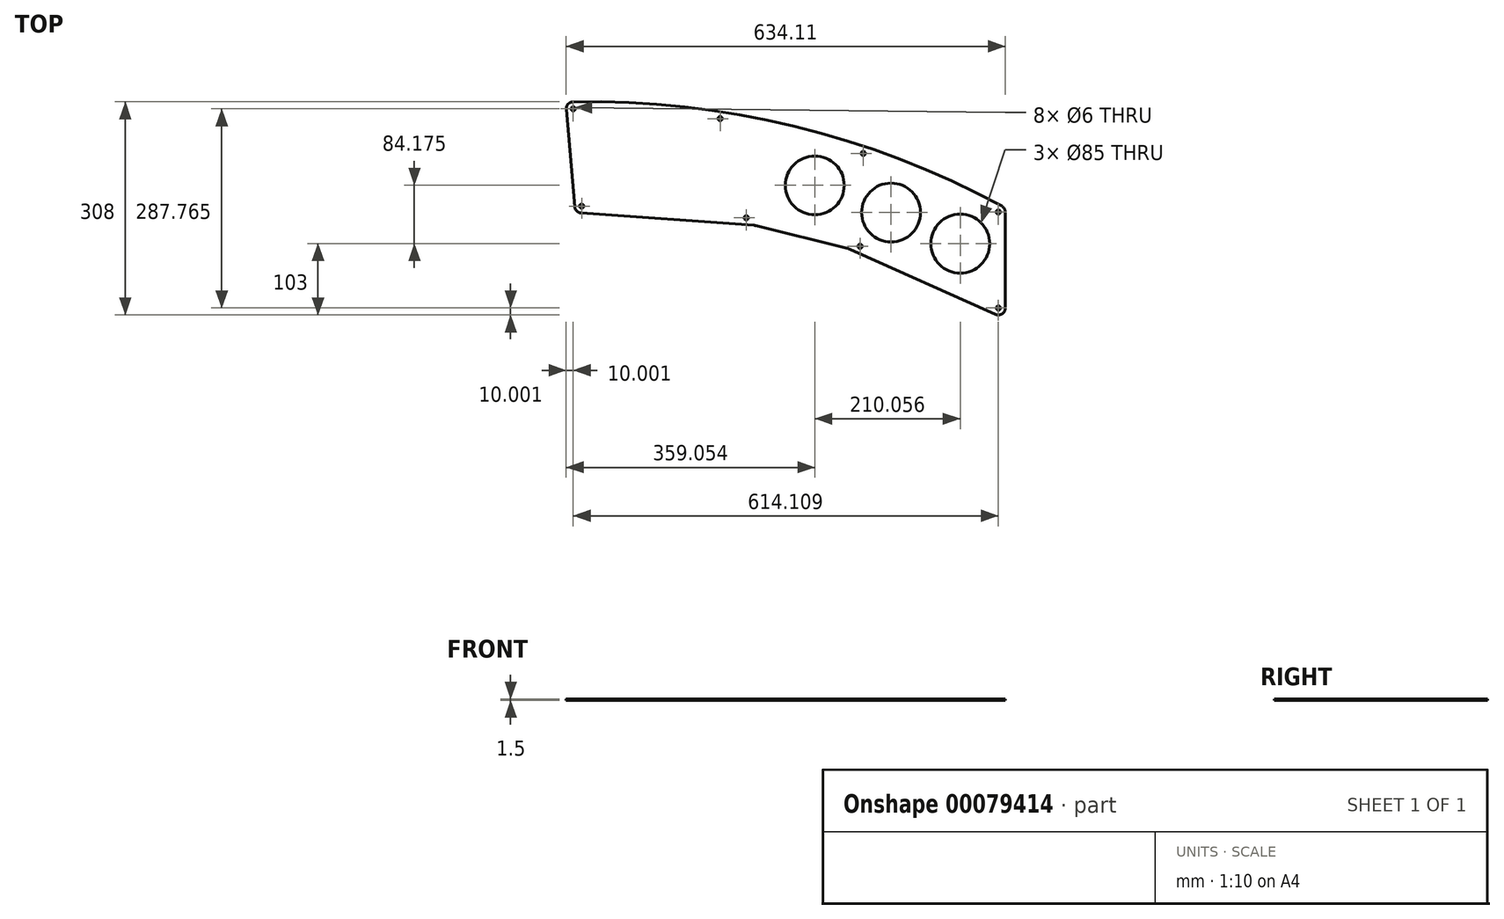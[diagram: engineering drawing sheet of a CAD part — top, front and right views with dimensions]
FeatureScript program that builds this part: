
annotation { "Feature Type Name" : "Feature", "Feature Type Description" : "" }
export const myFeature = defineFeature(function(context is Context, id is Id, definition is map)
    precondition{}
    {
        {
            var Q0;
            Q0=qCreatedBy(makeId("Top.planeOp"),FACE);
            var sketch = newSketch(context, id + "F0", { "sketchPlane" : qUnion([Q0])});
            skLineSegment(sketch, "E0", {"start": v(0, 450) * mm, "end": v(-635, 450) * mm});
            skLineSegment(sketch, "E1", {"start": v(-635, 450) * mm, "end": v(-635, 0) * mm});
            skLineSegment(sketch, "E2", {"start": v(-635, 0) * mm, "end": v(0, 0) * mm});
            skLineSegment(sketch, "E3", {"start": v(0, 0) * mm, "end": v(0, 450) * mm});
            skCircle(sketch, "E4", {"center": v(-600, -900) * mm, "radius": 1070 * mm});
            skCircle(sketch, "E5", {"center": v(-600, -900) * mm, "radius": 1250 * mm});
            skLineSegment(sketch, "E6", {"start": v(-621.03, 189.8) * mm, "end": v(-361.68, 171.41) * mm});
            skLineSegment(sketch, "E7", {"start": v(-361.68, 171.41) * mm, "end": v(-225.87, 137.41) * mm});
            skLineSegment(sketch, "E8", {"start": v(-225.87, 137.41) * mm, "end": v(0, 36.59) * mm});
            skPoint(sketch, "E9", {"position": v(0, 196.59) * mm});
            skLineSegment(sketch, "E10", {"start": v(-621.03, 189.8) * mm, "end": v(-635, 349.5) * mm});
            skSolve(sketch);
        }
        {
            var Q0;
            {var subQ8=sQuery(id+"F0.wireOp",EDGE,"E6");Q0=makeQuery(id+"F0.imprint","IMPRINT",FACE,{"disambiguationData":[TD([[makeQuery(id+"F0.imprint","IMPRINT",EDGE,{"derivedFrom":subQ8}),1.0]])]});}
            extrude(context, id + "F1", {"entities" : qUnion([Q0]), "depth" : 1.5 * mm});
        }
        {
            var Q0;
            Q0=makeQuery(id+"F1.opExtrude","CAP_FACE",FACE,{"disambiguationData":[OSD([sQuery(id+"F0.wireOp",EDGE,"E0"),sQuery(id+"F0.wireOp",EDGE,"E1"),sQuery(id+"F0.wireOp",EDGE,"E2"),sQuery(id+"F0.wireOp",EDGE,"NxOAb0fC-KCtt-g6Ye-Zb5N-PQVgE4h8CR18"),sQuery(id+"F0.wireOp",EDGE,"E3"),sQuery(id+"F0.wireOp",EDGE,"E4")])],"isStart":false});
            var sketch = newSketch(context, id + "F2", { "sketchPlane" : qUnion([Q0])});
            skCircle(sketch, "E11", {"center": v(-65, 145) * mm, "radius": 42.5 * mm});
            skCircle(sketch, "E12", {"center": v(-165, 190) * mm, "radius": 42.5 * mm});
            skCircle(sketch, "E13", {"center": v(-275.06, 229.18) * mm, "radius": 42.5 * mm});
            skLineSegment(sketch, "E14", {"start": v(-293.77, 154.41) * mm, "end": v(-256.83, 301.97) * mm, "construction": true});
            skCircle(sketch, "E15", {"center": v(-600, -900) * mm, "radius": 1175 * mm, "construction": true});
            skSolve(sketch);
        }
        {
            var Q0;
            Q0=makeQuery(id+"F2.imprint","IMPRINT",FACE,{"disambiguationData":[TD([[makeQuery(id+"F2.imprint","IMPRINT",EDGE,{"derivedFrom":sQuery(id+"F2.wireOp",EDGE,"E13")}),1.0]])]});
            var Q1;
            Q1=makeQuery(id+"F2.imprint","IMPRINT",FACE,{"disambiguationData":[TD([[makeQuery(id+"F2.imprint","IMPRINT",EDGE,{"derivedFrom":sQuery(id+"F2.wireOp",EDGE,"E12")}),1.0]])]});
            var Q2;
            Q2=makeQuery(id+"F2.imprint","IMPRINT",FACE,{"disambiguationData":[TD([[makeQuery(id+"F2.imprint","IMPRINT",EDGE,{"derivedFrom":sQuery(id+"F2.wireOp",EDGE,"E11")}),1.0]])]});
            extrude(context, id + "F3", {"entities" : qUnion([Q0, Q1, Q2]), "operationType" : NewBodyOperationType.REMOVE, "endBound" : BoundingType.THROUGH_ALL, "oppositeDirection" : true, "depth" : 25 * mm});
        }
        {
            var Q0;
            Q0=makeQuery(id+"F1.opExtrude","SWEPT_EDGE",EDGE,{"disambiguationData":[OSD([sQuery(id+"F0.wireOp",EDGE,"E3"),sQuery(id+"F0.wireOp",EDGE,"E5")])]});
            var Q1;
            Q1=makeQuery(id+"F1.opExtrude","SWEPT_EDGE",EDGE,{"disambiguationData":[OSD([sQuery(id+"F0.wireOp",EDGE,"E3"),sQuery(id+"F0.wireOp",EDGE,"E4")])]});
            var Q2;
            Q2=makeQuery(id+"F1.opExtrude","SWEPT_EDGE",EDGE,{"disambiguationData":[OSD([sQuery(id+"F0.wireOp",EDGE,"E1"),sQuery(id+"F0.wireOp",EDGE,"E5")])]});
            var Q3;
            Q3=makeQuery(id+"F1.opExtrude","SWEPT_EDGE",EDGE,{"disambiguationData":[OSD([sQuery(id+"F0.wireOp",EDGE,"E1"),sQuery(id+"F0.wireOp",EDGE,"E4")])]});
            var Q4;
            Q4=makeQuery(id+"F1.opExtrude","SWEPT_EDGE",EDGE,{"disambiguationData":[OSD([sQuery(id+"F0.wireOp",EDGE,"E6"),sQuery(id+"F0.wireOp",EDGE,"E10")])]});
            fillet(context, id + "F4", {"entities" : qUnion([Q0, Q1, Q2, Q3, Q4]), "radius" : 10 * mm, "tangentPropagation" : true, "allowEdgeOverflow" : false});
        }
        {
            var Q0;
            Q0=makeQuery(id+"F1.opExtrude","SWEPT_EDGE",EDGE,{"disambiguationData":[OSD([sQuery(id+"F0.wireOp",EDGE,"E6"),sQuery(id+"F0.wireOp",EDGE,"E7")])]});
            var Q1;
            Q1=makeQuery(id+"F1.opExtrude","SWEPT_EDGE",EDGE,{"disambiguationData":[OSD([sQuery(id+"F0.wireOp",EDGE,"E7"),sQuery(id+"F0.wireOp",EDGE,"E8")])]});
            fillet(context, id + "F5", {"entities" : qUnion([Q0, Q1]), "radius" : 20 * mm, "tangentPropagation" : true, "allowEdgeOverflow" : false});
        }
        {
            var Q0;
            Q0=makeQuery(id+"F1.opExtrude","CAP_FACE",FACE,{"disambiguationData":[OSD([sQuery(id+"F0.wireOp",EDGE,"E3"),sQuery(id+"F0.wireOp",EDGE,"E5"),sQuery(id+"F0.wireOp",EDGE,"E6"),sQuery(id+"F0.wireOp",EDGE,"E7"),sQuery(id+"F0.wireOp",EDGE,"E8"),sQuery(id+"F0.wireOp",EDGE,"E10")])],"isStart":false});
            var sketch = newSketch(context, id + "F6", { "sketchPlane" : qUnion([Q0])});
            skCircle(sketch, "E16", {"center": v(-624.1, 339.77) * mm, "radius": 3 * mm});
            skCircle(sketch, "E17", {"center": v(-611.8, 199.17) * mm, "radius": 3 * mm});
            skCircle(sketch, "E18", {"center": v(-10, 190.64) * mm, "radius": 3 * mm});
            skCircle(sketch, "E19", {"center": v(-10, 52) * mm, "radius": 3 * mm});
            skCircle(sketch, "E20", {"center": v(-600, -900) * mm, "radius": 1240 * mm, "construction": true});
            skLineSegment(sketch, "E21", {"start": v(-600, -900) * mm, "end": v(-411.84, 325.64) * mm, "construction": true});
            skCircle(sketch, "E22", {"center": v(-205.1, 275.44) * mm, "radius": 3 * mm});
            skCircle(sketch, "E23", {"center": v(-209.8, 141.2) * mm, "radius": 3 * mm});
            skCircle(sketch, "E24", {"center": v(-374.06, 182.31) * mm, "radius": 3 * mm});
            skCircle(sketch, "E25", {"center": v(-411.84, 325.64) * mm, "radius": 3 * mm});
            skLineSegment(sketch, "E26", {"start": v(-600, -900) * mm, "end": v(-205.1, 275.44) * mm, "construction": true});
            skLineSegment(sketch, "E27", {"start": v(-600, -900) * mm, "end": v(-624.1, 339.77) * mm, "construction": true});
            skLineSegment(sketch, "E28", {"start": v(-600, -900) * mm, "end": v(-10, 190.64) * mm, "construction": true});
            skLineSegment(sketch, "E29", {"start": v(-624.1, 339.77) * mm, "end": v(-411.84, 325.64) * mm, "construction": true});
            skLineSegment(sketch, "E30", {"start": v(-205.1, 275.44) * mm, "end": v(-411.84, 325.64) * mm, "construction": true});
            skLineSegment(sketch, "E31", {"start": v(-205.1, 275.44) * mm, "end": v(-10, 190.64) * mm, "construction": true});
            skLineSegment(sketch, "E32.0", {"start": v(-220.2, 145.83) * mm, "end": v(-12.82, 53.26) * mm, "construction": true});
            skLineSegment(sketch, "E32.1", {"start": v(-610.1, 199.05) * mm, "end": v(-362.72, 181.5) * mm, "construction": true});
            skArc(sketch, "E32.2", {"start": v(-362.72, 181.5) * mm, "mid": v(-360.12, 181.21) * mm, "end": v(-357.55, 180.69) * mm, "construction": true});
            skLineSegment(sketch, "E32.3", {"start": v(-357.55, 180.69) * mm, "end": v(-225.14, 147.54) * mm, "construction": true});
            skArc(sketch, "E32.4", {"start": v(-225.14, 147.54) * mm, "mid": v(-222.63, 146.8) * mm, "end": v(-220.2, 145.83) * mm, "construction": true});
            skLineSegment(sketch, "E33", {"start": v(-293.77, 154.41) * mm, "end": v(-275.06, 229.18) * mm, "construction": true});
            skSolve(sketch);
        }
        {
            var Q0;
            Q0=sQuery(id+"F6.wireOp",VERTEX,"E29.start");
            var Q1;
            Q1=sQuery(id+"F6.wireOp",VERTEX,"E17.center");
            var Q2;
            Q2=sQuery(id+"F6.wireOp",VERTEX,"E30.end");
            var Q3;
            Q3=sQuery(id+"F6.wireOp",VERTEX,"E24.center");
            var Q4;
            Q4=sQuery(id+"F6.wireOp",VERTEX,"E31.start");
            var Q5;
            Q5=sQuery(id+"F6.wireOp",VERTEX,"E23.center");
            var Q6;
            Q6=sQuery(id+"F6.wireOp",VERTEX,"E28.end");
            var Q7;
            Q7=sQuery(id+"F6.wireOp",VERTEX,"E19.center");
            var Q8;
            Q8=makeQuery(id+"F1.opExtrude","SWEPT_BODY",BODY,{"disambiguationData":[OSD([sQuery(id+"F0.wireOp",EDGE,"E3"),sQuery(id+"F0.wireOp",EDGE,"E5"),sQuery(id+"F0.wireOp",EDGE,"E6"),sQuery(id+"F0.wireOp",EDGE,"E7"),sQuery(id+"F0.wireOp",EDGE,"E8"),sQuery(id+"F0.wireOp",EDGE,"E10")])]});
            hole(context, id + "F7", {"style" : HoleStyle.SIMPLE, "endStyle" : HoleEndStyle.THROUGH, "holeDiameter" : 6 * mm, "locations" : qUnion([Q0, Q1, Q2, Q3, Q4, Q5, Q6, Q7]), "scope" : qUnion([Q8]), "isTappedThrough" : true});
        }
    });
